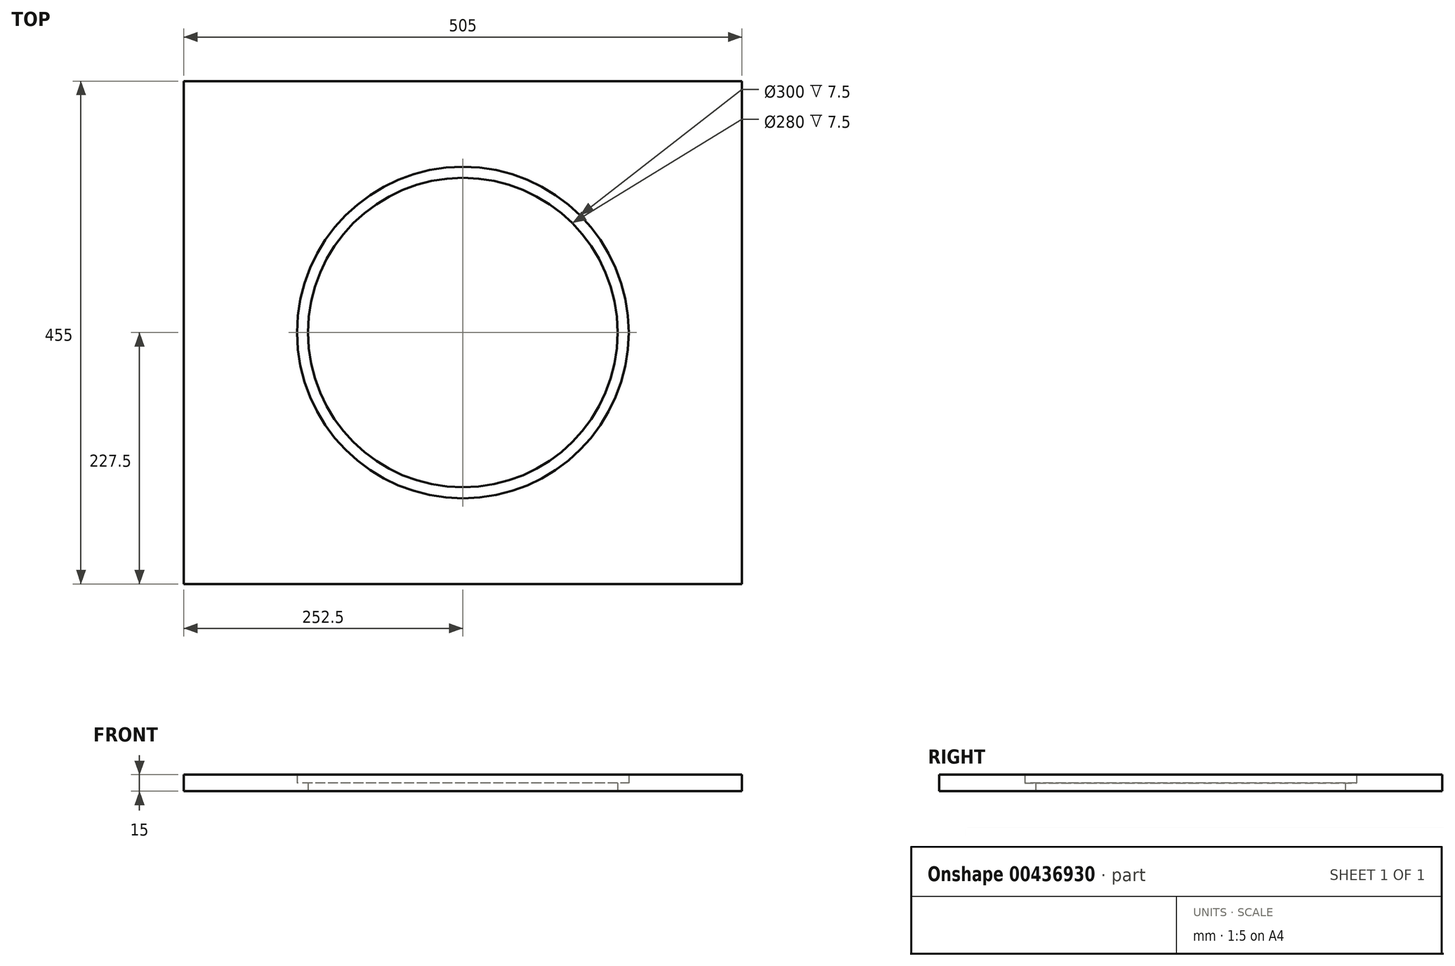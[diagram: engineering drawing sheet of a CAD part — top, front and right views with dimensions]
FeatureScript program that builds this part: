
annotation { "Feature Type Name" : "Feature", "Feature Type Description" : "" }
export const myFeature = defineFeature(function(context is Context, id is Id, definition is map)
    precondition{}
    {
        {
            var Q0;
            Q0=qCreatedBy(makeId("Top.planeOp"),FACE);
            var sketch = newSketch(context, id + "F0", { "sketchPlane" : qUnion([Q0])});
            skLineSegment(sketch, "E0.bottom", {"start": v(252.5, 227.5) * mm, "end": v(-252.5, 227.5) * mm});
            skLineSegment(sketch, "E0.top", {"start": v(252.5, -227.5) * mm, "end": v(-252.5, -227.5) * mm});
            skLineSegment(sketch, "E0.left", {"start": v(252.5, 227.5) * mm, "end": v(252.5, -227.5) * mm});
            skLineSegment(sketch, "E0.right", {"start": v(-252.5, 227.5) * mm, "end": v(-252.5, -227.5) * mm});
            skPoint(sketch, "E0.middle", {"position": v(0, 0) * mm});
            skCircle(sketch, "E1", {"center": v(0, 0) * mm, "radius": 150 * mm});
            skCircle(sketch, "E2", {"center": v(0, 0) * mm, "radius": 140 * mm});
            skSolve(sketch);
        }
        {
            var Q0;
            Q0=makeQuery(id+"F0.imprint","IMPRINT",FACE,{"disambiguationData":[TD([[makeQuery(id+"F0.imprint","IMPRINT",EDGE,{"derivedFrom":sQuery(id+"F0.wireOp",EDGE,"E0.bottom")}),1.0]])]});
            extrude(context, id + "F1", {"entities" : qUnion([Q0]), "depth" : 15 * mm});
        }
        {
            var Q0;
            Q0=makeQuery(id+"F0.imprint","IMPRINT",FACE,{"disambiguationData":[TD([[makeQuery(id+"F0.imprint","IMPRINT",EDGE,{"derivedFrom":sQuery(id+"F0.wireOp",EDGE,"E1")}),1.0]])]});
            extrude(context, id + "F2", {"entities" : qUnion([Q0]), "operationType" : NewBodyOperationType.ADD, "depth" : 7.5 * mm});
        }
    });
